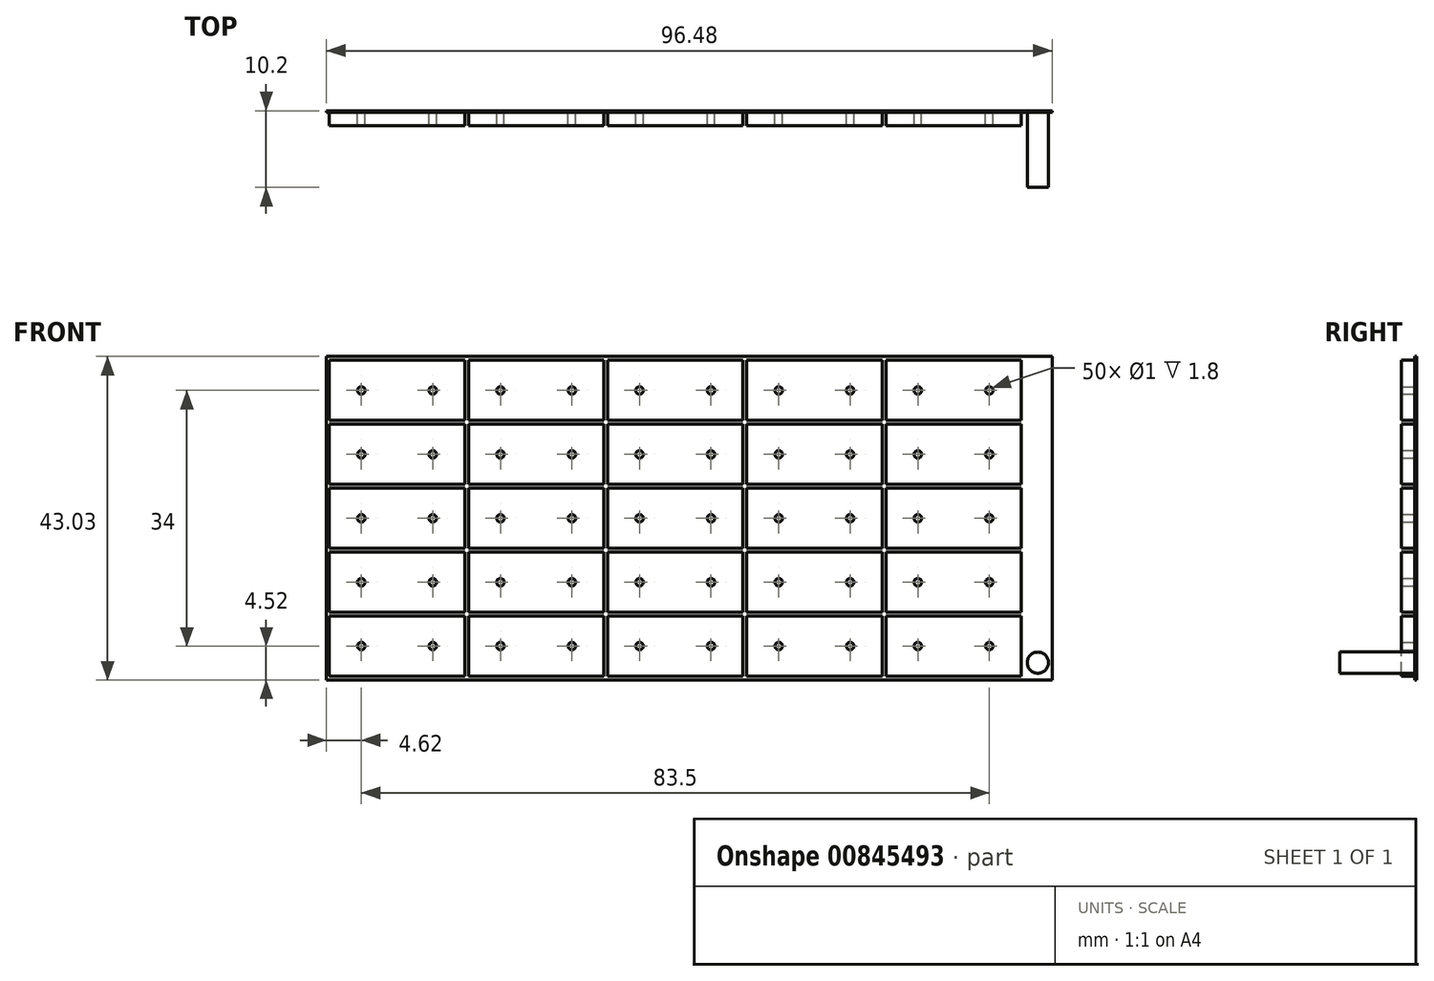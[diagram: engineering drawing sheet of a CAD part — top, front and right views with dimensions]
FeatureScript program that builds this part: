
annotation { "Feature Type Name" : "Feature", "Feature Type Description" : "" }
export const myFeature = defineFeature(function(context is Context, id is Id, definition is map)
    precondition{}
    {
        {
            var Q0;
            Q0=qCreatedBy(makeId("Front.planeOp"),FACE);
            var sketch = newSketch(context, id + "F0", { "sketchPlane" : qUnion([Q0])});
            skLineSegment(sketch, "E0.bottom", {"start": v(9, -4) * mm, "end": v(-9, -4) * mm});
            skLineSegment(sketch, "E0.top", {"start": v(9, 4) * mm, "end": v(-9, 4) * mm});
            skLineSegment(sketch, "E0.left", {"start": v(9, -4) * mm, "end": v(9, 4) * mm});
            skLineSegment(sketch, "E0.right", {"start": v(-9, -4) * mm, "end": v(-9, 4) * mm});
            skPoint(sketch, "E0.middle", {"position": v(0, 0) * mm});
            skCircle(sketch, "E1", {"center": v(-4.75, 0) * mm, "radius": 0.5 * mm});
            skCircle(sketch, "E2", {"center": v(4.75, 0) * mm, "radius": 0.5 * mm});
            skPoint(sketch, "E3.0.1.0", {"position": v(0, 8.5) * mm});
            skLineSegment(sketch, "E3.0.1.1", {"start": v(-9, 4.5) * mm, "end": v(-9, 12.5) * mm});
            skLineSegment(sketch, "E3.0.1.2", {"start": v(9, 4.5) * mm, "end": v(9, 12.5) * mm});
            skLineSegment(sketch, "E3.0.1.3", {"start": v(9, 12.5) * mm, "end": v(-9, 12.5) * mm});
            skLineSegment(sketch, "E3.0.1.4", {"start": v(9, 4.5) * mm, "end": v(-9, 4.5) * mm});
            skCircle(sketch, "E3.0.1.5", {"center": v(4.75, 8.5) * mm, "radius": 0.5 * mm});
            skCircle(sketch, "E3.0.1.6", {"center": v(-4.75, 8.5) * mm, "radius": 0.5 * mm});
            skPoint(sketch, "E3.0.2.0", {"position": v(0, 17) * mm});
            skLineSegment(sketch, "E3.0.2.1", {"start": v(-9, 13) * mm, "end": v(-9, 21) * mm});
            skLineSegment(sketch, "E3.0.2.2", {"start": v(9, 13) * mm, "end": v(9, 21) * mm});
            skLineSegment(sketch, "E3.0.2.3", {"start": v(9, 21) * mm, "end": v(-9, 21) * mm});
            skLineSegment(sketch, "E3.0.2.4", {"start": v(9, 13) * mm, "end": v(-9, 13) * mm});
            skCircle(sketch, "E3.0.2.5", {"center": v(4.75, 17) * mm, "radius": 0.5 * mm});
            skCircle(sketch, "E3.0.2.6", {"center": v(-4.75, 17) * mm, "radius": 0.5 * mm});
            skPoint(sketch, "E3.0.3.0", {"position": v(0, 25.5) * mm});
            skLineSegment(sketch, "E3.0.3.1", {"start": v(-9, 21.5) * mm, "end": v(-9, 29.5) * mm});
            skLineSegment(sketch, "E3.0.3.2", {"start": v(9, 21.5) * mm, "end": v(9, 29.5) * mm});
            skLineSegment(sketch, "E3.0.3.3", {"start": v(9, 29.5) * mm, "end": v(-9, 29.5) * mm});
            skLineSegment(sketch, "E3.0.3.4", {"start": v(9, 21.5) * mm, "end": v(-9, 21.5) * mm});
            skCircle(sketch, "E3.0.3.5", {"center": v(4.75, 25.5) * mm, "radius": 0.5 * mm});
            skCircle(sketch, "E3.0.3.6", {"center": v(-4.75, 25.5) * mm, "radius": 0.5 * mm});
            skPoint(sketch, "E3.0.4.0", {"position": v(0, 34) * mm});
            skLineSegment(sketch, "E3.0.4.1", {"start": v(-9, 30) * mm, "end": v(-9, 38) * mm});
            skLineSegment(sketch, "E3.0.4.2", {"start": v(9, 30) * mm, "end": v(9, 38) * mm});
            skLineSegment(sketch, "E3.0.4.3", {"start": v(9, 38) * mm, "end": v(-9, 38) * mm});
            skLineSegment(sketch, "E3.0.4.4", {"start": v(9, 30) * mm, "end": v(-9, 30) * mm});
            skCircle(sketch, "E3.0.4.5", {"center": v(4.75, 34) * mm, "radius": 0.5 * mm});
            skCircle(sketch, "E3.0.4.6", {"center": v(-4.75, 34) * mm, "radius": 0.5 * mm});
            skPoint(sketch, "E3.1.0.0", {"position": v(18.5, 0) * mm});
            skLineSegment(sketch, "E3.1.0.1", {"start": v(9.5, -4) * mm, "end": v(9.5, 4) * mm});
            skLineSegment(sketch, "E3.1.0.2", {"start": v(27.5, -4) * mm, "end": v(27.5, 4) * mm});
            skLineSegment(sketch, "E3.1.0.3", {"start": v(27.5, 4) * mm, "end": v(9.5, 4) * mm});
            skLineSegment(sketch, "E3.1.0.4", {"start": v(27.5, -4) * mm, "end": v(9.5, -4) * mm});
            skCircle(sketch, "E3.1.0.5", {"center": v(23.25, 0) * mm, "radius": 0.5 * mm});
            skCircle(sketch, "E3.1.0.6", {"center": v(13.75, 0) * mm, "radius": 0.5 * mm});
            skPoint(sketch, "E3.1.1.0", {"position": v(18.5, 8.5) * mm});
            skLineSegment(sketch, "E3.1.1.1", {"start": v(9.5, 4.5) * mm, "end": v(9.5, 12.5) * mm});
            skLineSegment(sketch, "E3.1.1.2", {"start": v(27.5, 4.5) * mm, "end": v(27.5, 12.5) * mm});
            skLineSegment(sketch, "E3.1.1.3", {"start": v(27.5, 12.5) * mm, "end": v(9.5, 12.5) * mm});
            skLineSegment(sketch, "E3.1.1.4", {"start": v(27.5, 4.5) * mm, "end": v(9.5, 4.5) * mm});
            skCircle(sketch, "E3.1.1.5", {"center": v(23.25, 8.5) * mm, "radius": 0.5 * mm});
            skCircle(sketch, "E3.1.1.6", {"center": v(13.75, 8.5) * mm, "radius": 0.5 * mm});
            skPoint(sketch, "E3.1.2.0", {"position": v(18.5, 17) * mm});
            skLineSegment(sketch, "E3.1.2.1", {"start": v(9.5, 13) * mm, "end": v(9.5, 21) * mm});
            skLineSegment(sketch, "E3.1.2.2", {"start": v(27.5, 13) * mm, "end": v(27.5, 21) * mm});
            skLineSegment(sketch, "E3.1.2.3", {"start": v(27.5, 21) * mm, "end": v(9.5, 21) * mm});
            skLineSegment(sketch, "E3.1.2.4", {"start": v(27.5, 13) * mm, "end": v(9.5, 13) * mm});
            skCircle(sketch, "E3.1.2.5", {"center": v(23.25, 17) * mm, "radius": 0.5 * mm});
            skCircle(sketch, "E3.1.2.6", {"center": v(13.75, 17) * mm, "radius": 0.5 * mm});
            skPoint(sketch, "E3.1.3.0", {"position": v(18.5, 25.5) * mm});
            skLineSegment(sketch, "E3.1.3.1", {"start": v(9.5, 21.5) * mm, "end": v(9.5, 29.5) * mm});
            skLineSegment(sketch, "E3.1.3.2", {"start": v(27.5, 21.5) * mm, "end": v(27.5, 29.5) * mm});
            skLineSegment(sketch, "E3.1.3.3", {"start": v(27.5, 29.5) * mm, "end": v(9.5, 29.5) * mm});
            skLineSegment(sketch, "E3.1.3.4", {"start": v(27.5, 21.5) * mm, "end": v(9.5, 21.5) * mm});
            skCircle(sketch, "E3.1.3.5", {"center": v(23.25, 25.5) * mm, "radius": 0.5 * mm});
            skCircle(sketch, "E3.1.3.6", {"center": v(13.75, 25.5) * mm, "radius": 0.5 * mm});
            skPoint(sketch, "E3.1.4.0", {"position": v(18.5, 34) * mm});
            skLineSegment(sketch, "E3.1.4.1", {"start": v(9.5, 30) * mm, "end": v(9.5, 38) * mm});
            skLineSegment(sketch, "E3.1.4.2", {"start": v(27.5, 30) * mm, "end": v(27.5, 38) * mm});
            skLineSegment(sketch, "E3.1.4.3", {"start": v(27.5, 38) * mm, "end": v(9.5, 38) * mm});
            skLineSegment(sketch, "E3.1.4.4", {"start": v(27.5, 30) * mm, "end": v(9.5, 30) * mm});
            skCircle(sketch, "E3.1.4.5", {"center": v(23.25, 34) * mm, "radius": 0.5 * mm});
            skCircle(sketch, "E3.1.4.6", {"center": v(13.75, 34) * mm, "radius": 0.5 * mm});
            skPoint(sketch, "E3.2.0.0", {"position": v(37, 0) * mm});
            skLineSegment(sketch, "E3.2.0.1", {"start": v(28, -4) * mm, "end": v(28, 4) * mm});
            skLineSegment(sketch, "E3.2.0.2", {"start": v(46, -4) * mm, "end": v(46, 4) * mm});
            skLineSegment(sketch, "E3.2.0.3", {"start": v(46, 4) * mm, "end": v(28, 4) * mm});
            skLineSegment(sketch, "E3.2.0.4", {"start": v(46, -4) * mm, "end": v(28, -4) * mm});
            skCircle(sketch, "E3.2.0.5", {"center": v(41.75, 0) * mm, "radius": 0.5 * mm});
            skCircle(sketch, "E3.2.0.6", {"center": v(32.25, 0) * mm, "radius": 0.5 * mm});
            skPoint(sketch, "E3.2.1.0", {"position": v(37, 8.5) * mm});
            skLineSegment(sketch, "E3.2.1.1", {"start": v(28, 4.5) * mm, "end": v(28, 12.5) * mm});
            skLineSegment(sketch, "E3.2.1.2", {"start": v(46, 4.5) * mm, "end": v(46, 12.5) * mm});
            skLineSegment(sketch, "E3.2.1.3", {"start": v(46, 12.5) * mm, "end": v(28, 12.5) * mm});
            skLineSegment(sketch, "E3.2.1.4", {"start": v(46, 4.5) * mm, "end": v(28, 4.5) * mm});
            skCircle(sketch, "E3.2.1.5", {"center": v(41.75, 8.5) * mm, "radius": 0.5 * mm});
            skCircle(sketch, "E3.2.1.6", {"center": v(32.25, 8.5) * mm, "radius": 0.5 * mm});
            skPoint(sketch, "E3.2.2.0", {"position": v(37, 17) * mm});
            skLineSegment(sketch, "E3.2.2.1", {"start": v(28, 13) * mm, "end": v(28, 21) * mm});
            skLineSegment(sketch, "E3.2.2.2", {"start": v(46, 13) * mm, "end": v(46, 21) * mm});
            skLineSegment(sketch, "E3.2.2.3", {"start": v(46, 21) * mm, "end": v(28, 21) * mm});
            skLineSegment(sketch, "E3.2.2.4", {"start": v(46, 13) * mm, "end": v(28, 13) * mm});
            skCircle(sketch, "E3.2.2.5", {"center": v(41.75, 17) * mm, "radius": 0.5 * mm});
            skCircle(sketch, "E3.2.2.6", {"center": v(32.25, 17) * mm, "radius": 0.5 * mm});
            skPoint(sketch, "E3.2.3.0", {"position": v(37, 25.5) * mm});
            skLineSegment(sketch, "E3.2.3.1", {"start": v(28, 21.5) * mm, "end": v(28, 29.5) * mm});
            skLineSegment(sketch, "E3.2.3.2", {"start": v(46, 21.5) * mm, "end": v(46, 29.5) * mm});
            skLineSegment(sketch, "E3.2.3.3", {"start": v(46, 29.5) * mm, "end": v(28, 29.5) * mm});
            skLineSegment(sketch, "E3.2.3.4", {"start": v(46, 21.5) * mm, "end": v(28, 21.5) * mm});
            skCircle(sketch, "E3.2.3.5", {"center": v(41.75, 25.5) * mm, "radius": 0.5 * mm});
            skCircle(sketch, "E3.2.3.6", {"center": v(32.25, 25.5) * mm, "radius": 0.5 * mm});
            skPoint(sketch, "E3.2.4.0", {"position": v(37, 34) * mm});
            skLineSegment(sketch, "E3.2.4.1", {"start": v(28, 30) * mm, "end": v(28, 38) * mm});
            skLineSegment(sketch, "E3.2.4.2", {"start": v(46, 30) * mm, "end": v(46, 38) * mm});
            skLineSegment(sketch, "E3.2.4.3", {"start": v(46, 38) * mm, "end": v(28, 38) * mm});
            skLineSegment(sketch, "E3.2.4.4", {"start": v(46, 30) * mm, "end": v(28, 30) * mm});
            skCircle(sketch, "E3.2.4.5", {"center": v(41.75, 34) * mm, "radius": 0.5 * mm});
            skCircle(sketch, "E3.2.4.6", {"center": v(32.25, 34) * mm, "radius": 0.5 * mm});
            skPoint(sketch, "E3.3.0.0", {"position": v(55.5, 0) * mm});
            skLineSegment(sketch, "E3.3.0.1", {"start": v(46.5, -4) * mm, "end": v(46.5, 4) * mm});
            skLineSegment(sketch, "E3.3.0.2", {"start": v(64.5, -4) * mm, "end": v(64.5, 4) * mm});
            skLineSegment(sketch, "E3.3.0.3", {"start": v(64.5, 4) * mm, "end": v(46.5, 4) * mm});
            skLineSegment(sketch, "E3.3.0.4", {"start": v(64.5, -4) * mm, "end": v(46.5, -4) * mm});
            skCircle(sketch, "E3.3.0.5", {"center": v(60.25, 0) * mm, "radius": 0.5 * mm});
            skCircle(sketch, "E3.3.0.6", {"center": v(50.75, 0) * mm, "radius": 0.5 * mm});
            skPoint(sketch, "E3.3.1.0", {"position": v(55.5, 8.5) * mm});
            skLineSegment(sketch, "E3.3.1.1", {"start": v(46.5, 4.5) * mm, "end": v(46.5, 12.5) * mm});
            skLineSegment(sketch, "E3.3.1.2", {"start": v(64.5, 4.5) * mm, "end": v(64.5, 12.5) * mm});
            skLineSegment(sketch, "E3.3.1.3", {"start": v(64.5, 12.5) * mm, "end": v(46.5, 12.5) * mm});
            skLineSegment(sketch, "E3.3.1.4", {"start": v(64.5, 4.5) * mm, "end": v(46.5, 4.5) * mm});
            skCircle(sketch, "E3.3.1.5", {"center": v(60.25, 8.5) * mm, "radius": 0.5 * mm});
            skCircle(sketch, "E3.3.1.6", {"center": v(50.75, 8.5) * mm, "radius": 0.5 * mm});
            skPoint(sketch, "E3.3.2.0", {"position": v(55.5, 17) * mm});
            skLineSegment(sketch, "E3.3.2.1", {"start": v(46.5, 13) * mm, "end": v(46.5, 21) * mm});
            skLineSegment(sketch, "E3.3.2.2", {"start": v(64.5, 13) * mm, "end": v(64.5, 21) * mm});
            skLineSegment(sketch, "E3.3.2.3", {"start": v(64.5, 21) * mm, "end": v(46.5, 21) * mm});
            skLineSegment(sketch, "E3.3.2.4", {"start": v(64.5, 13) * mm, "end": v(46.5, 13) * mm});
            skCircle(sketch, "E3.3.2.5", {"center": v(60.25, 17) * mm, "radius": 0.5 * mm});
            skCircle(sketch, "E3.3.2.6", {"center": v(50.75, 17) * mm, "radius": 0.5 * mm});
            skPoint(sketch, "E3.3.3.0", {"position": v(55.5, 25.5) * mm});
            skLineSegment(sketch, "E3.3.3.1", {"start": v(46.5, 21.5) * mm, "end": v(46.5, 29.5) * mm});
            skLineSegment(sketch, "E3.3.3.2", {"start": v(64.5, 21.5) * mm, "end": v(64.5, 29.5) * mm});
            skLineSegment(sketch, "E3.3.3.3", {"start": v(64.5, 29.5) * mm, "end": v(46.5, 29.5) * mm});
            skLineSegment(sketch, "E3.3.3.4", {"start": v(64.5, 21.5) * mm, "end": v(46.5, 21.5) * mm});
            skCircle(sketch, "E3.3.3.5", {"center": v(60.25, 25.5) * mm, "radius": 0.5 * mm});
            skCircle(sketch, "E3.3.3.6", {"center": v(50.75, 25.5) * mm, "radius": 0.5 * mm});
            skPoint(sketch, "E3.3.4.0", {"position": v(55.5, 34) * mm});
            skLineSegment(sketch, "E3.3.4.1", {"start": v(46.5, 30) * mm, "end": v(46.5, 38) * mm});
            skLineSegment(sketch, "E3.3.4.2", {"start": v(64.5, 30) * mm, "end": v(64.5, 38) * mm});
            skLineSegment(sketch, "E3.3.4.3", {"start": v(64.5, 38) * mm, "end": v(46.5, 38) * mm});
            skLineSegment(sketch, "E3.3.4.4", {"start": v(64.5, 30) * mm, "end": v(46.5, 30) * mm});
            skCircle(sketch, "E3.3.4.5", {"center": v(60.25, 34) * mm, "radius": 0.5 * mm});
            skCircle(sketch, "E3.3.4.6", {"center": v(50.75, 34) * mm, "radius": 0.5 * mm});
            skPoint(sketch, "E3.4.0.0", {"position": v(74, 0) * mm});
            skLineSegment(sketch, "E3.4.0.1", {"start": v(65, -4) * mm, "end": v(65, 4) * mm});
            skLineSegment(sketch, "E3.4.0.2", {"start": v(83, -4) * mm, "end": v(83, 4) * mm});
            skLineSegment(sketch, "E3.4.0.3", {"start": v(83, 4) * mm, "end": v(65, 4) * mm});
            skLineSegment(sketch, "E3.4.0.4", {"start": v(83, -4) * mm, "end": v(65, -4) * mm});
            skCircle(sketch, "E3.4.0.5", {"center": v(78.75, 0) * mm, "radius": 0.5 * mm});
            skCircle(sketch, "E3.4.0.6", {"center": v(69.25, 0) * mm, "radius": 0.5 * mm});
            skPoint(sketch, "E3.4.1.0", {"position": v(74, 8.5) * mm});
            skLineSegment(sketch, "E3.4.1.1", {"start": v(65, 4.5) * mm, "end": v(65, 12.5) * mm});
            skLineSegment(sketch, "E3.4.1.2", {"start": v(83, 4.5) * mm, "end": v(83, 12.5) * mm});
            skLineSegment(sketch, "E3.4.1.3", {"start": v(83, 12.5) * mm, "end": v(65, 12.5) * mm});
            skLineSegment(sketch, "E3.4.1.4", {"start": v(83, 4.5) * mm, "end": v(65, 4.5) * mm});
            skCircle(sketch, "E3.4.1.5", {"center": v(78.75, 8.5) * mm, "radius": 0.5 * mm});
            skCircle(sketch, "E3.4.1.6", {"center": v(69.25, 8.5) * mm, "radius": 0.5 * mm});
            skPoint(sketch, "E3.4.2.0", {"position": v(74, 17) * mm});
            skLineSegment(sketch, "E3.4.2.1", {"start": v(65, 13) * mm, "end": v(65, 21) * mm});
            skLineSegment(sketch, "E3.4.2.2", {"start": v(83, 13) * mm, "end": v(83, 21) * mm});
            skLineSegment(sketch, "E3.4.2.3", {"start": v(83, 21) * mm, "end": v(65, 21) * mm});
            skLineSegment(sketch, "E3.4.2.4", {"start": v(83, 13) * mm, "end": v(65, 13) * mm});
            skCircle(sketch, "E3.4.2.5", {"center": v(78.75, 17) * mm, "radius": 0.5 * mm});
            skCircle(sketch, "E3.4.2.6", {"center": v(69.25, 17) * mm, "radius": 0.5 * mm});
            skPoint(sketch, "E3.4.3.0", {"position": v(74, 25.5) * mm});
            skLineSegment(sketch, "E3.4.3.1", {"start": v(65, 21.5) * mm, "end": v(65, 29.5) * mm});
            skLineSegment(sketch, "E3.4.3.2", {"start": v(83, 21.5) * mm, "end": v(83, 29.5) * mm});
            skLineSegment(sketch, "E3.4.3.3", {"start": v(83, 29.5) * mm, "end": v(65, 29.5) * mm});
            skLineSegment(sketch, "E3.4.3.4", {"start": v(83, 21.5) * mm, "end": v(65, 21.5) * mm});
            skCircle(sketch, "E3.4.3.5", {"center": v(78.75, 25.5) * mm, "radius": 0.5 * mm});
            skCircle(sketch, "E3.4.3.6", {"center": v(69.25, 25.5) * mm, "radius": 0.5 * mm});
            skPoint(sketch, "E3.4.4.0", {"position": v(74, 34) * mm});
            skLineSegment(sketch, "E3.4.4.1", {"start": v(65, 30) * mm, "end": v(65, 38) * mm});
            skLineSegment(sketch, "E3.4.4.2", {"start": v(83, 30) * mm, "end": v(83, 38) * mm});
            skLineSegment(sketch, "E3.4.4.3", {"start": v(83, 38) * mm, "end": v(65, 38) * mm});
            skLineSegment(sketch, "E3.4.4.4", {"start": v(83, 30) * mm, "end": v(65, 30) * mm});
            skCircle(sketch, "E3.4.4.5", {"center": v(78.75, 34) * mm, "radius": 0.5 * mm});
            skCircle(sketch, "E3.4.4.6", {"center": v(69.25, 34) * mm, "radius": 0.5 * mm});
            skLineSegment(sketch, "E3.direction1", {"start": v(-9, -4) * mm, "end": v(9.5, -4) * mm, "construction": true});
            skLineSegment(sketch, "E3.direction2", {"start": v(-9, -4) * mm, "end": v(-9, 4.5) * mm, "construction": true});
            skSolve(sketch);
        }
        {
            var Q0;
            Q0=qCreatedBy(makeId("Front.planeOp"),FACE);
            var sketch = newSketch(context, id + "F1", { "sketchPlane" : qUnion([Q0])});
            skPoint(sketch, "E4.middle", {"position": v(0, 0) * mm});
            skLineSegment(sketch, "E5.bottom", {"start": v(-9.37, -4.52) * mm, "end": v(87.1, -4.52) * mm});
            skLineSegment(sketch, "E5.top", {"start": v(-9.37, 38.51) * mm, "end": v(87.1, 38.51) * mm});
            skLineSegment(sketch, "E5.left", {"start": v(-9.37, -4.52) * mm, "end": v(-9.37, 38.51) * mm});
            skLineSegment(sketch, "E5.right", {"start": v(87.1, -4.52) * mm, "end": v(87.1, 38.51) * mm});
            skSolve(sketch);
        }
        {
            var Q0;
            Q0 = qSketchRegion(id + "F1", true);
            extrude(context, id + "F2", {"entities" : qUnion([Q0]), "depth" : 0.2 * mm, "offsetDistance" : 25 * mm});
        }
        {
            var Q0;
            Q0=makeQuery(id+"F2.opExtrude","CAP_FACE",FACE,{"disambiguationData":[OSD([sQuery(id+"F1.wireOp",EDGE,"E5.bottom"),sQuery(id+"F1.wireOp",EDGE,"E5.top"),sQuery(id+"F1.wireOp",EDGE,"E5.left"),sQuery(id+"F1.wireOp",EDGE,"E5.right")])],"isStart":false});
            var sketch = newSketch(context, id + "F3", { "sketchPlane" : qUnion([Q0])});
            skCircle(sketch, "E6", {"center": v(85.2, -2.2) * mm, "radius": 1.4 * mm});
            skSolve(sketch);
        }
        {
            var Q0;
            Q0 = qSketchRegion(id + "F3", true);
            extrude(context, id + "F4", {"entities" : qUnion([Q0]), "operationType" : NewBodyOperationType.ADD, "depth" : 10 * mm, "offsetDistance" : 25 * mm});
        }
        {
            var Q0;
            Q0 = qSketchRegion(id + "F0", true);
            extrude(context, id + "F5", {"entities" : qUnion([Q0]), "operationType" : NewBodyOperationType.ADD, "depth" : 2 * mm, "offsetDistance" : 25 * mm});
        }
    });
